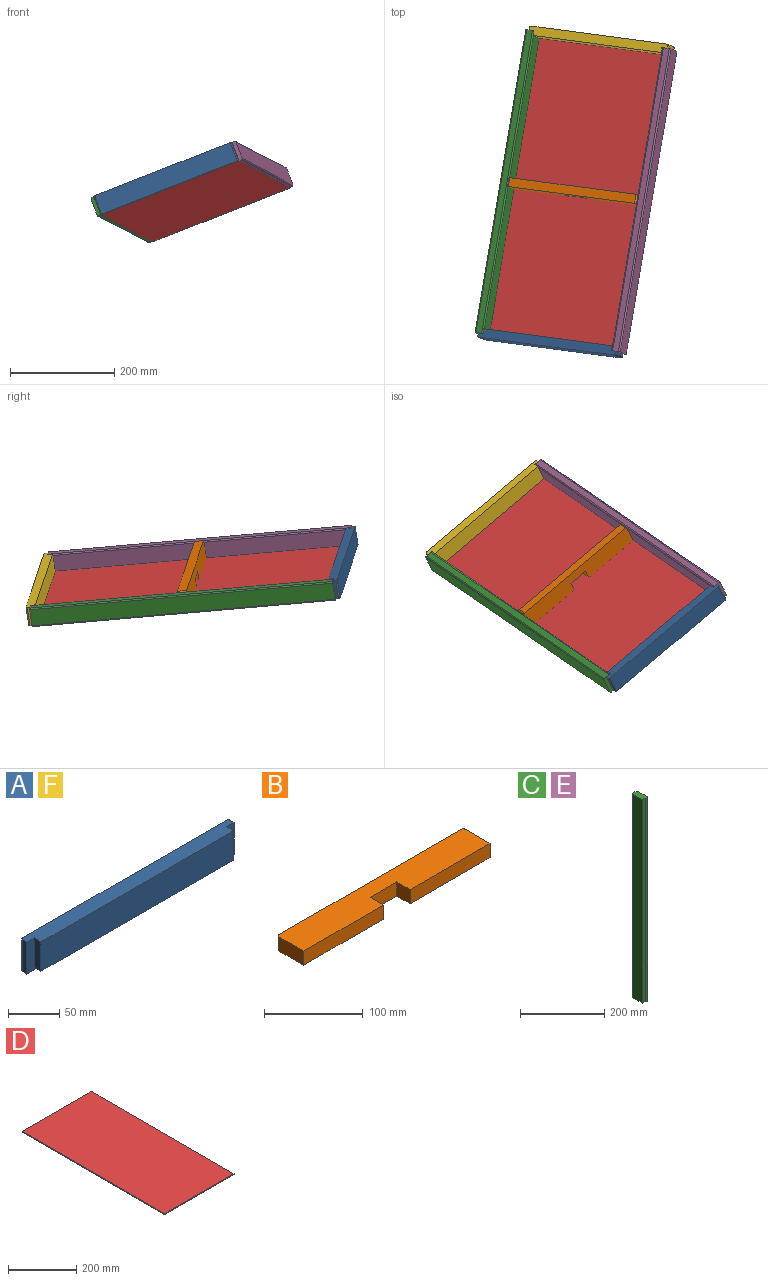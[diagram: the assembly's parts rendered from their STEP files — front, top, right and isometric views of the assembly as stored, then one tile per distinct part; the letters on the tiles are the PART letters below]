
ASSEMBLY  parts=6 mates=8
PART A: 12 faces, bbox 285.8x17.5x38.1 mm
  f0: plane 34.93x9.53mm, normal (-1,0,0), area 332.7mm2, adj f1,f8,f9,f11
  f1: plane 265.43x34.93mm, normal (0,-1,0), area 9270.1mm2, adj f0,f7,f9,f11
  f2: plane 38.1x5.41mm, normal (1,0,0), area 206.1mm2, adj f3,f8,f9,f10
  f3: cylinder r=2.54mm len=38.1mm, axis (0,0,-1), area 152mm2, adj f2,f4,f9,f10
  f4: plane 280.67x38.1mm, normal (0,1,0), area 10693.5mm2, adj f3,f5,f9,f10
  f5: cylinder r=2.54mm len=38.1mm, axis (0,0,-1), area 152mm2, adj f4,f6,f9,f10
  f6: plane 38.1x5.41mm, normal (-1,0,0), area 206.1mm2, adj f5,f8,f9,f10
  f7: plane 34.93x9.53mm, normal (1,0,0), area 332.7mm2, adj f1,f8,f9,f11
  f8: plane 285.75x38.1mm, normal (0,-1,0), area 1616.9mm2, adj f0,f2,f6,f7,f9,f10,f11
  f9: plane 285.75x17.48mm, normal (0,0,1), area 4797.2mm2, adj f0,f1,f2,f3,f4,f5,f6,f7
  f10: plane 285.75x7.95mm, normal (0,0,-1), area 2269mm2, adj f2,f3,f4,f5,f6,f8
  f11: plane 265.43x9.53mm, normal (0,0,-1), area 2528.2mm2, adj f0,f1,f7,f8
PART B: 12 faces, bbox 266.7x38.1x17.5 mm
  f0: plane 38.1x17.48mm, normal (0,-1,0), area 665.8mm2, adj f1,f9,f10,f11
  f1: plane 19.05x17.48mm, normal (-1,0,0), area 332.9mm2, adj f0,f2,f10,f11
  f2: plane 114.3x17.48mm, normal (0,-1,0), area 1997.4mm2, adj f1,f3,f10,f11
  f3: plane 35.56x17.48mm, normal (1,0,0), area 621.4mm2, adj f2,f4,f10,f11
  f4: cylinder r=2.54mm len=17.48mm, axis (0,0,-1), area 69.7mm2, adj f3,f5,f10,f11
  f5: plane 261.62x17.48mm, normal (0,1,0), area 4571.9mm2, adj f4,f6,f10,f11
  f6: cylinder r=2.54mm len=17.48mm, axis (0,0,-1), area 69.7mm2, adj f5,f7,f10,f11
  f7: plane 35.56x17.48mm, normal (-1,0,0), area 621.4mm2, adj f6,f8,f10,f11
  f8: plane 114.3x17.48mm, normal (0,-1,0), area 1997.4mm2, adj f7,f9,f10,f11
  f9: plane 19.05x17.48mm, normal (1,0,0), area 332.9mm2, adj f0,f8,f10,f11
  f10: plane 266.7x38.1mm, normal (0,0,1), area 9432.7mm2, adj f0,f1,f2,f3,f4,f5,f6,f7
  f11: plane 266.7x38.1mm, normal (0,0,-1), area 9432.7mm2, adj f0,f1,f2,f3,f4,f5,f6,f7
PART C: 11 faces, bbox 17x38.1x590.6 mm
  f0: plane 590.55x33.02mm, normal (1,0,0), area 19500mm2, adj f1,f8,f9,f10
  f1: cylinder r=2.54mm len=590.55mm, axis (0,0,-1), area 2356.2mm2, adj f0,f2,f9,f10
  f2: plane 590.55x11.89mm, normal (0,1,0), area 7020mm2, adj f1,f3,f9,f10
  f3: cylinder r=2.54mm len=590.55mm, axis (0,0,-1), area 2356.2mm2, adj f2,f4,f9,f10
  f4: plane 590.55x32.39mm, normal (-1,0,0), area 19125mm2, adj f3,f5,f9,f10
  f5: plane 590.55x9.53mm, normal (0,-1,0), area 5625mm2, adj f4,f6,f9,f10
  f6: plane 590.55x3.18mm, normal (-1,0,0), area 1875mm2, adj f5,f7,f9,f10
  f7: plane 590.55x4.9mm, normal (0,-1,0), area 2895mm2, adj f6,f8,f9,f10
  f8: cylinder r=2.54mm len=590.55mm, axis (0,0,-1), area 2356.2mm2, adj f0,f7,f9,f10
  f9: plane 38.1x16.97mm, normal (0,0,1), area 612.1mm2, adj f0,f1,f2,f3,f4,f5,f6,f7
  f10: plane 38.1x16.97mm, normal (0,0,-1), area 612.1mm2, adj f0,f1,f2,f3,f4,f5,f6,f7
PART D: 6 faces, bbox 285.8x590.6x3.2 mm
  f0: plane 285.75x3.18mm, normal (0,1,0), area 907.3mm2, adj f1,f3,f4,f5
  f1: plane 590.55x3.18mm, normal (-1,0,0), area 1875mm2, adj f0,f2,f4,f5
  f2: plane 285.75x3.18mm, normal (0,-1,0), area 907.3mm2, adj f1,f3,f4,f5
  f3: plane 590.55x3.18mm, normal (1,0,0), area 1875mm2, adj f0,f2,f4,f5
  f4: plane 590.55x285.75mm, normal (0,0,1), area 168749.7mm2, adj f0,f1,f2,f3
  f5: plane 590.55x285.75mm, normal (0,0,-1), area 168749.7mm2, adj f0,f1,f2,f3
PART E: same geometry as C
PART F: same geometry as A
PLACE A rot(axis=(-0.18,0.06,0.98),171.6deg) t=(-111.49,-731.84,-7.71)mm
PLACE B rot(axis=(0.96,-0.26,0.11),85.7deg) t=(-221.29,-414.68,-18.89)mm
PLACE C rot(axis=(-0.08,0.75,0.66),159.2deg) t=(-382.41,-703.14,-88.15)mm
PLACE D rot(axis=(-0.28,-0.89,-0.36),23.5deg) t=(-184.7,-421.79,-81.73)mm
PLACE E rot(axis=(0.96,-0.26,0.11),85.7deg) t=(-19.24,-158.32,-34.45)mm
PLACE F rot(axis=(-0.28,-0.89,-0.36),23.5deg) t=(-274.01,-136.12,-158.1)mm
MATE parallel F.f10 <-> D.f5  axis (-0.35,0.14,0.93) through (-12.14,-161.44,-56.44)mm
MATE parallel F.f10 <-> D.f4  axis (-0.35,0.14,0.93) through (-12.14,-161.44,-56.44)mm
MATE parallel A.f10 <-> D.f4  axis (-0.35,0.14,0.93) through (-109.49,-741.68,-5.49)mm
MATE parallel F.f10 <-> D.f4  axis (-0.35,0.14,0.93) through (-11.25,-156.12,-56.9)mm
MATE parallel A.f10 <-> D.f5  axis (-0.35,0.14,0.93) through (-109.49,-741.68,-5.49)mm
MATE parallel C.f6 <-> D.f1  axis (0.92,-0.12,0.36) through (-373.36,-706.53,-109.37)mm
MATE parallel B.f3 <-> E.f4  axis (0.92,-0.12,0.36) through (-76.32,-447.68,-16.46)mm
MATE parallel E.f6 <-> D.f3  axis (-0.92,0.12,-0.36) through (-110.04,-741.45,-4.02)mm
